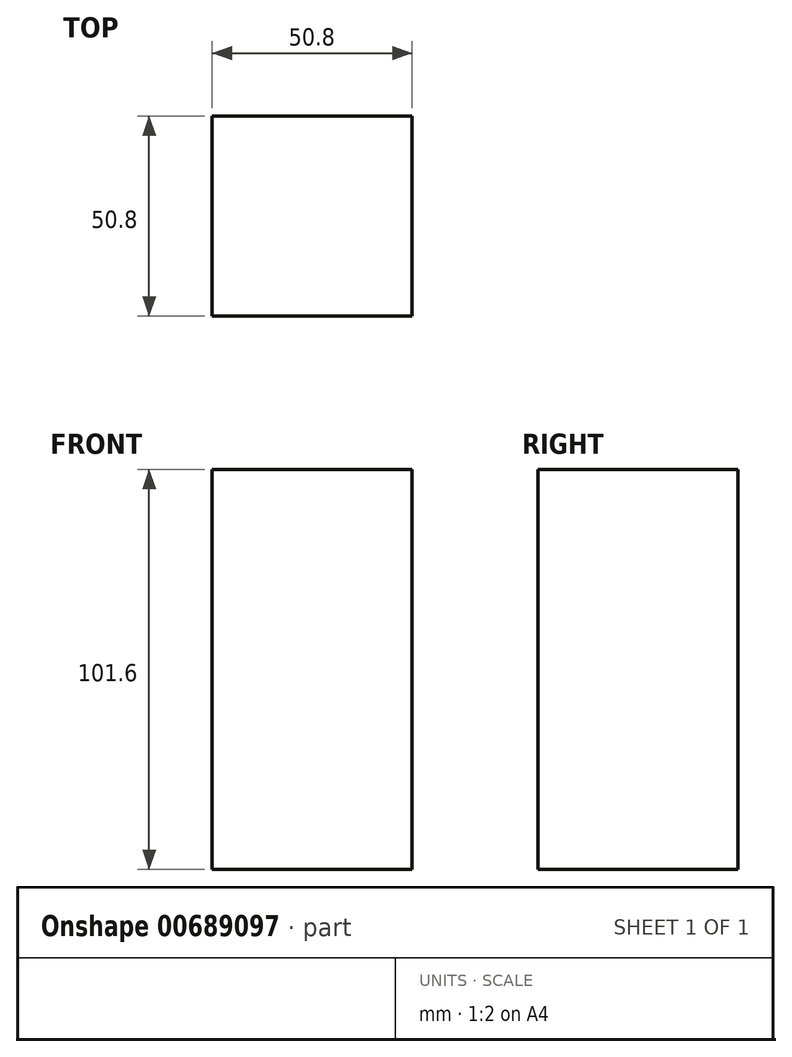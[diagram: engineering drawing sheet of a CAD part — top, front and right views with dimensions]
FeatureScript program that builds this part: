
annotation { "Feature Type Name" : "Feature", "Feature Type Description" : "" }
export const myFeature = defineFeature(function(context is Context, id is Id, definition is map)
    precondition{}
    {
        {
            var Q0;
            Q0=qCreatedBy(makeId("Front.planeOp"),FACE);
            var sketch = newSketch(context, id + "F0", { "sketchPlane" : qUnion([Q0])});
            skLineSegment(sketch, "E0.bottom", {"start": v(-50.8, 43.5) * mm, "end": v(0, 43.5) * mm});
            skLineSegment(sketch, "E0.top", {"start": v(-50.8, -58.1) * mm, "end": v(0, -58.1) * mm});
            skLineSegment(sketch, "E0.left", {"start": v(-50.8, 43.5) * mm, "end": v(-50.8, -58.1) * mm});
            skLineSegment(sketch, "E0.right", {"start": v(0, 43.5) * mm, "end": v(0, -58.1) * mm});
            skSolve(sketch);
        }
        {
            var Q0;
            Q0=makeQuery(id+"F0.imprint","IMPRINT",FACE,{"disambiguationData":[TD([[makeQuery(id+"F0.imprint","IMPRINT",EDGE,{"derivedFrom":sQuery(id+"F0.wireOp",EDGE,"E0.bottom")}),-1.0]])]});
            extrude(context, id + "F1", {"entities" : qUnion([Q0]), "endBound" : BoundingType.SYMMETRIC, "depth" : 50.8 * mm, "offsetDistance" : 25.4 * mm});
        }
    });
